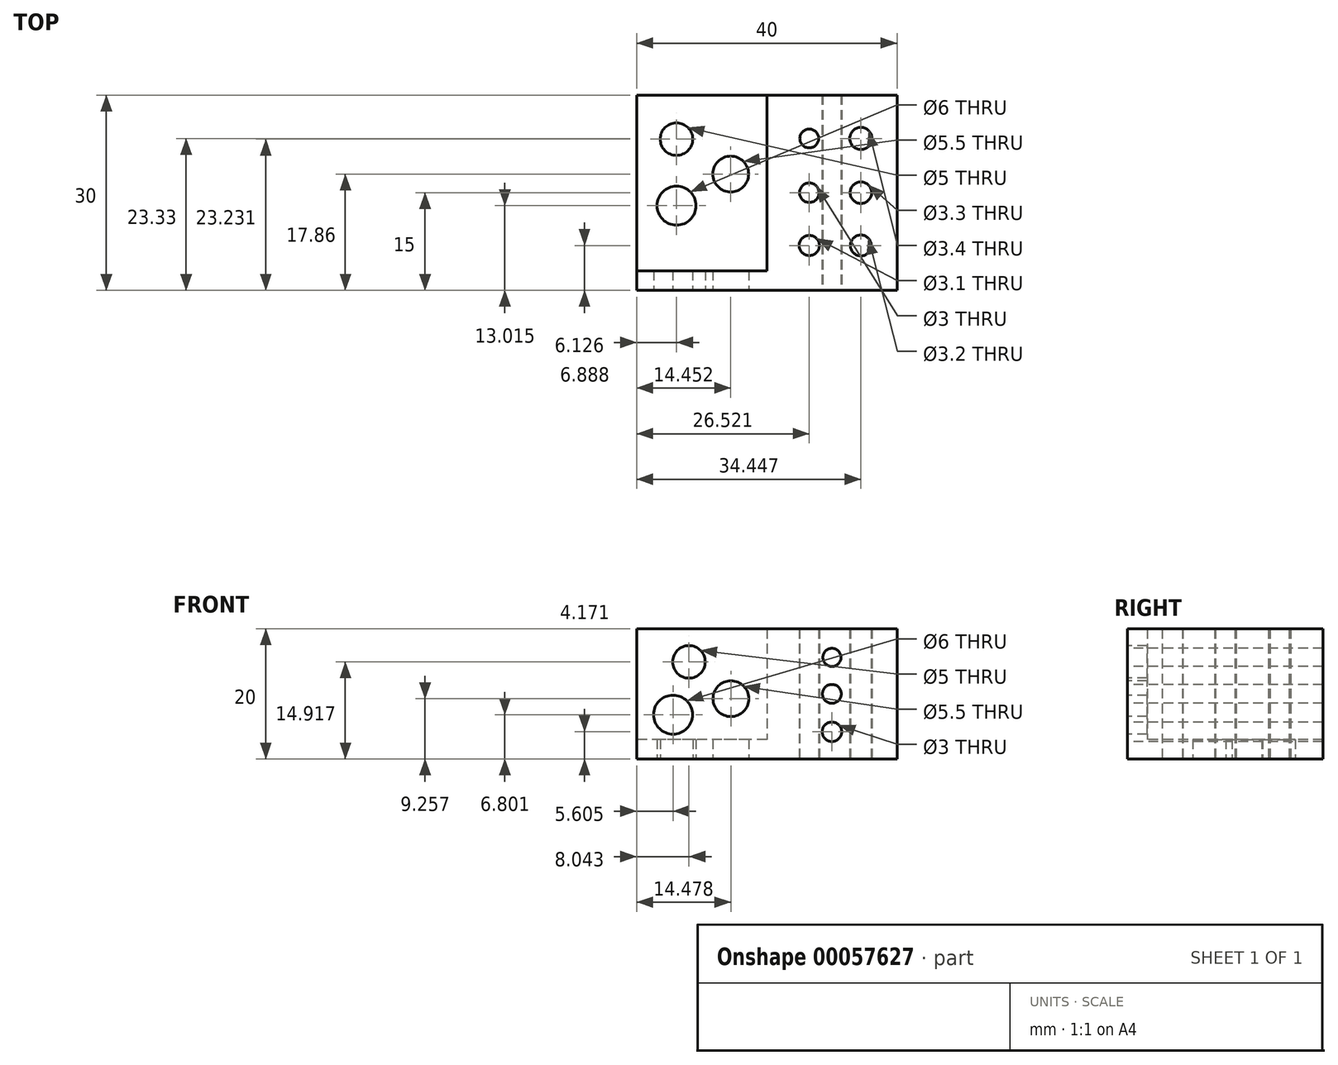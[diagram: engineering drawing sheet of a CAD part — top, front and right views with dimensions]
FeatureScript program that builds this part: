
annotation { "Feature Type Name" : "Feature", "Feature Type Description" : "" }
export const myFeature = defineFeature(function(context is Context, id is Id, definition is map)
    precondition{}
    {
        {
            var Q0;
            Q0=qCreatedBy(makeId("Top.planeOp"),FACE);
            var sketch = newSketch(context, id + "F0", { "sketchPlane" : qUnion([Q0])});
            skLineSegment(sketch, "E0.rect.bottom", {"start": v(20, -15) * mm, "end": v(-20, -15) * mm});
            skLineSegment(sketch, "E0.rect.top", {"start": v(20, 15) * mm, "end": v(-20, 15) * mm});
            skLineSegment(sketch, "E0.rect.left", {"start": v(20, -15) * mm, "end": v(20, 15) * mm});
            skLineSegment(sketch, "E0.rect.right", {"start": v(-20, -15) * mm, "end": v(-20, 15) * mm});
            skPoint(sketch, "E0.rect.middle", {"position": v(0, 0) * mm});
            skLineSegment(sketch, "E1", {"start": v(0, 15) * mm, "end": v(0, -15) * mm});
            skCircle(sketch, "E2", {"center": v(-13.87, 8.23) * mm, "radius": 2.5 * mm});
            skCircle(sketch, "E3", {"center": v(-5.55, 2.86) * mm, "radius": 2.75 * mm});
            skCircle(sketch, "E4", {"center": v(-13.87, -1.99) * mm, "radius": 3 * mm});
            skLineSegment(sketch, "E5", {"start": v(6.52, 15) * mm, "end": v(6.52, -15) * mm, "construction": true});
            skCircle(sketch, "E6", {"center": v(6.52, 8.33) * mm, "radius": 1.45 * mm});
            skCircle(sketch, "E7", {"center": v(6.52, 0) * mm, "radius": 1.5 * mm});
            skCircle(sketch, "E8", {"center": v(6.52, -8.11) * mm, "radius": 1.55 * mm});
            skLineSegment(sketch, "E9", {"start": v(14.45, 15) * mm, "end": v(14.45, -15) * mm, "construction": true});
            skCircle(sketch, "E10", {"center": v(14.45, 8.33) * mm, "radius": 1.7 * mm});
            skCircle(sketch, "E11", {"center": v(14.45, 0) * mm, "radius": 1.65 * mm});
            skCircle(sketch, "E12", {"center": v(14.45, -8.11) * mm, "radius": 1.6 * mm});
            skLineSegment(sketch, "E13", {"start": v(0, -12) * mm, "end": v(-20, -12) * mm});
            skSolve(sketch);
        }
        {
            var Q0;
            Q0=makeQuery(id+"F0.imprint","IMPRINT",FACE,{"disambiguationData":[TD([[makeQuery(id+"F0.imprint","IMPRINT",EDGE,{"derivedFrom":sQuery(id+"F0.wireOp",EDGE,"E2")}),-1.0]])]});
            extrude(context, id + "F1", {"entities" : qUnion([Q0]), "depth" : 3 * mm});
        }
        {
            var Q0;
            {var subQ1=sQuery(id+"F0.wireOp",EDGE,"E0.rect.left");Q0=makeQuery(id+"F0.imprint","IMPRINT",FACE,{"disambiguationData":[TD([[makeQuery(id+"F0.imprint","IMPRINT",EDGE,{"derivedFrom":subQ1}),1.0]])]});}
            extrude(context, id + "F2", {"entities" : qUnion([Q0]), "operationType" : NewBodyOperationType.ADD, "depth" : 20 * mm});
        }
        {
            var Q0;
            {var subQ5=sQuery(id+"F0.wireOp",EDGE,"E13");Q0=makeQuery(id+"F0.imprint","IMPRINT",FACE,{"disambiguationData":[TD([[makeQuery(id+"F0.imprint","IMPRINT",EDGE,{"derivedFrom":subQ5}),1.0]])]});}
            var Q1;
            Q1=makeQuery(id+"F2.opExtrude","CAP_FACE",FACE,{"disambiguationData":[OSD([sQuery(id+"F0.wireOp",EDGE,"E0.rect.bottom"),sQuery(id+"F0.wireOp",EDGE,"E0.rect.top"),sQuery(id+"F0.wireOp",EDGE,"E0.rect.left"),sQuery(id+"F0.wireOp",EDGE,"E1"),sQuery(id+"F0.wireOp",EDGE,"E6"),sQuery(id+"F0.wireOp",EDGE,"E7"),sQuery(id+"F0.wireOp",EDGE,"E8"),sQuery(id+"F0.wireOp",EDGE,"E10"),sQuery(id+"F0.wireOp",EDGE,"E11"),sQuery(id+"F0.wireOp",EDGE,"E12")])],"isStart":false});
            extrude(context, id + "F3", {"entities" : qUnion([Q0]), "operationType" : NewBodyOperationType.ADD, "endBound" : BoundingType.UP_TO_SURFACE, "endBoundEntityFace" : qUnion([Q1]), "depth" : 25 * mm});
        }
        {
            var Q0;
            {var subQ0=sQuery(id+"F0.wireOp",EDGE,"E0.rect.bottom");Q0=makeQuery(id+"F3.boolean.opBoolean","MERGE",FACE,{"derivedFrom":[makeQuery(id+"F2.opExtrude","SWEPT_FACE",FACE,{"disambiguationData":[OSD([subQ0])]}),makeQuery(id+"F3.opExtrude","SWEPT_FACE",FACE,{"disambiguationData":[OSD([subQ0])]})]});}
            var sketch = newSketch(context, id + "F4", { "sketchPlane" : qUnion([Q0])});
            skCircle(sketch, "E14", {"center": v(-11.96, 14.92) * mm, "radius": 2.5 * mm});
            skCircle(sketch, "E15", {"center": v(-5.52, 9.26) * mm, "radius": 2.75 * mm});
            skCircle(sketch, "E16", {"center": v(-14.4, 6.8) * mm, "radius": 3 * mm});
            skCircle(sketch, "E17", {"center": v(10, 15.6) * mm, "radius": 1.4 * mm});
            skCircle(sketch, "E18", {"center": v(10, 10) * mm, "radius": 1.45 * mm});
            skCircle(sketch, "E19", {"center": v(10, 4.17) * mm, "radius": 1.5 * mm});
            skLineSegment(sketch, "E20.0", {"start": v(20, 20) * mm, "end": v(0, 20) * mm});
            skLineSegment(sketch, "E21", {"start": v(10, 20) * mm, "end": v(10, 0) * mm, "construction": true});
            skSolve(sketch);
        }
        {
            var Q0;
            Q0=makeQuery(id+"F4.imprint","IMPRINT",FACE,{"disambiguationData":[TD([[makeQuery(id+"F4.imprint","IMPRINT",EDGE,{"derivedFrom":sQuery(id+"F4.wireOp",EDGE,"E17")}),1.0]])]});
            var Q1;
            Q1=makeQuery(id+"F4.imprint","IMPRINT",FACE,{"disambiguationData":[TD([[makeQuery(id+"F4.imprint","IMPRINT",EDGE,{"derivedFrom":sQuery(id+"F4.wireOp",EDGE,"E18")}),1.0]])]});
            var Q2;
            Q2=makeQuery(id+"F4.imprint","IMPRINT",FACE,{"disambiguationData":[TD([[makeQuery(id+"F4.imprint","IMPRINT",EDGE,{"derivedFrom":sQuery(id+"F4.wireOp",EDGE,"E19")}),1.0]])]});
            var Q3;
            Q3=makeQuery(id+"F4.imprint","IMPRINT",FACE,{"disambiguationData":[TD([[makeQuery(id+"F4.imprint","IMPRINT",EDGE,{"derivedFrom":sQuery(id+"F4.wireOp",EDGE,"E15")}),1.0]])]});
            var Q4;
            Q4=makeQuery(id+"F4.imprint","IMPRINT",FACE,{"disambiguationData":[TD([[makeQuery(id+"F4.imprint","IMPRINT",EDGE,{"derivedFrom":sQuery(id+"F4.wireOp",EDGE,"E14")}),1.0]])]});
            var Q5;
            Q5=makeQuery(id+"F4.imprint","IMPRINT",FACE,{"disambiguationData":[TD([[makeQuery(id+"F4.imprint","IMPRINT",EDGE,{"derivedFrom":sQuery(id+"F4.wireOp",EDGE,"E16")}),1.0]])]});
            var Q6;
            {var subQ0=sQuery(id+"F0.wireOp",EDGE,"E0.rect.top");Q6=makeQuery(id+"F2.boolean.opBoolean","MERGE",FACE,{"derivedFrom":[makeQuery(id+"F1.opExtrude","SWEPT_FACE",FACE,{"disambiguationData":[OSD([subQ0])]}),makeQuery(id+"F2.opExtrude","SWEPT_FACE",FACE,{"disambiguationData":[OSD([subQ0])]})]});}
            extrude(context, id + "F5", {"entities" : qUnion([Q0, Q1, Q2, Q3, Q4, Q5]), "operationType" : NewBodyOperationType.REMOVE, "endBound" : BoundingType.UP_TO_SURFACE, "oppositeDirection" : true, "endBoundEntityFace" : qUnion([Q6]), "depth" : 25 * mm});
        }
    });
